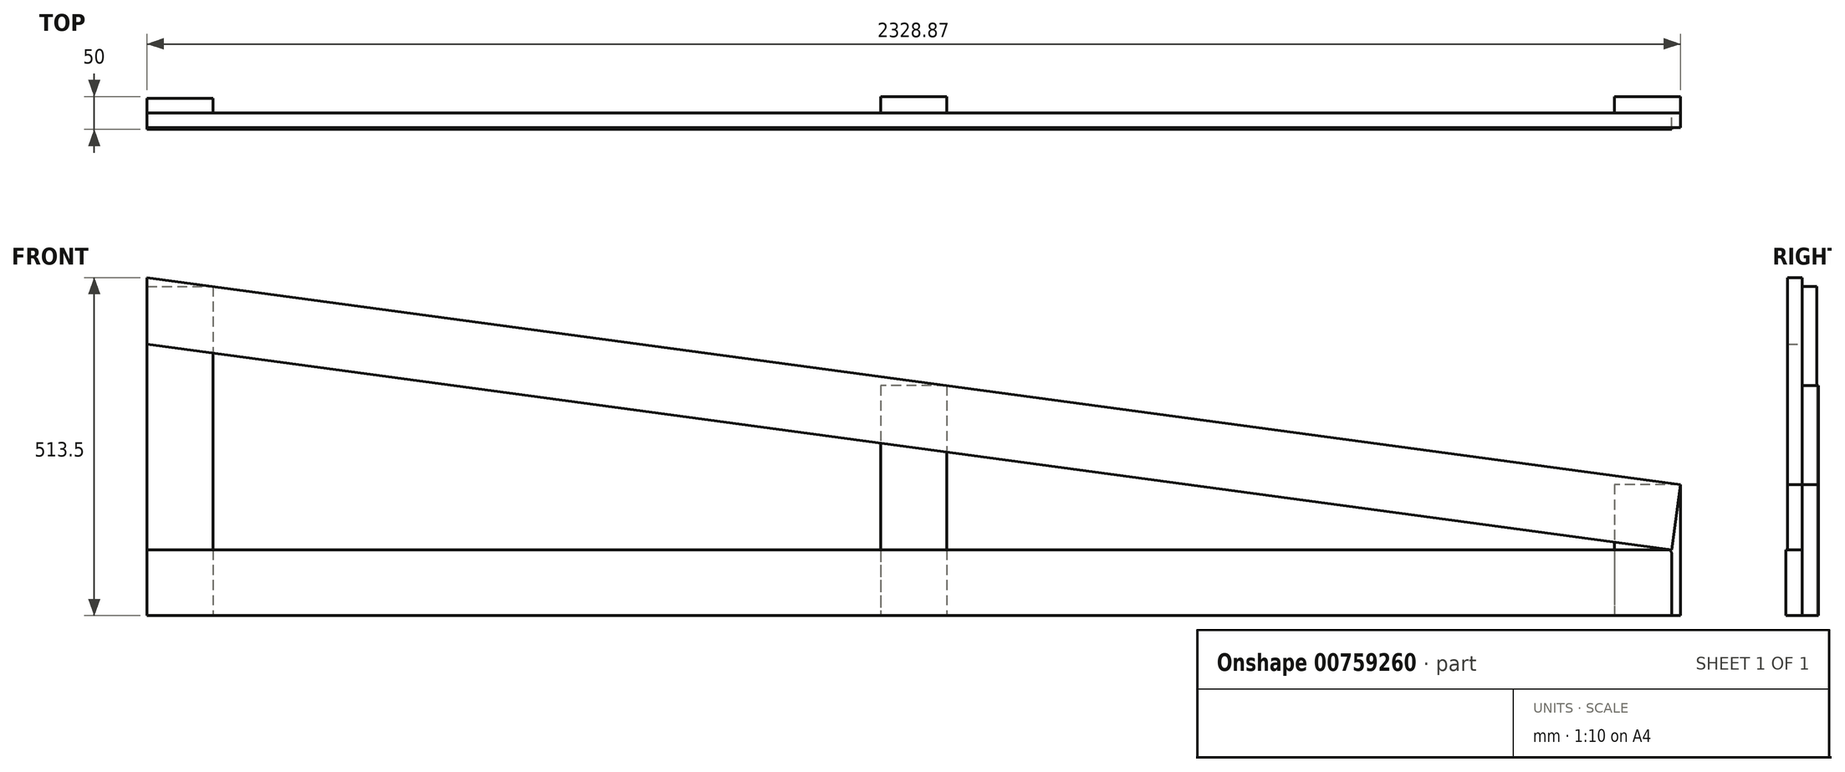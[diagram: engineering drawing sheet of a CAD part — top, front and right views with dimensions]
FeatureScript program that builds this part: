
annotation { "Feature Type Name" : "Feature", "Feature Type Description" : "" }
export const myFeature = defineFeature(function(context is Context, id is Id, definition is map)
    precondition{}
    {
        {
            var Q0;
            Q0=qCreatedBy(makeId("Front.planeOp"),FACE);
            var sketch = newSketch(context, id + "F0", { "sketchPlane" : qUnion([Q0])});
            skLineSegment(sketch, "E0.bottom", {"start": v(0, 500) * mm, "end": v(100, 500) * mm});
            skLineSegment(sketch, "E0.top", {"start": v(0, 0) * mm, "end": v(100, 0) * mm});
            skLineSegment(sketch, "E0.left", {"start": v(0, 500) * mm, "end": v(0, 0) * mm});
            skLineSegment(sketch, "E0.right", {"start": v(100, 500) * mm, "end": v(100, 0) * mm});
            skSolve(sketch);
        }
        {
            var Q0;
            Q0 = qSketchRegion(id + "F0", true);
            extrude(context, id + "F1", {"entities" : qUnion([Q0]), "depth" : 22 * mm, "offsetDistance" : 25 * mm});
        }
        {
            var Q0;
            Q0=makeQuery(id+"F1.opExtrude","CAP_FACE",FACE,{"disambiguationData":[OSD([sQuery(id+"F0.wireOp",EDGE,"E0.bottom"),sQuery(id+"F0.wireOp",EDGE,"E0.top"),sQuery(id+"F0.wireOp",EDGE,"E0.left"),sQuery(id+"F0.wireOp",EDGE,"E0.right")])],"isStart":false});
            var sketch = newSketch(context, id + "F2", { "sketchPlane" : qUnion([Q0])});
            skLineSegment(sketch, "E1", {"start": v(0, 412.6) * mm, "end": v(2315.5, 100) * mm});
            skLineSegment(sketch, "E2", {"start": v(2315.5, 100) * mm, "end": v(2328.87, 199.1) * mm});
            skLineSegment(sketch, "E3", {"start": v(2328.87, 199.1) * mm, "end": v(0, 513.5) * mm});
            skLineSegment(sketch, "E4", {"start": v(0, 513.5) * mm, "end": v(0, 412.6) * mm});
            skLineSegment(sketch, "E5", {"start": v(0, 0) * mm, "end": v(2315.5, 0) * mm});
            skPoint(sketch, "E5.endSnap0", {"position": v(50, 0) * mm});
            skLineSegment(sketch, "E6", {"start": v(2315.5, 0) * mm, "end": v(2315.5, 95) * mm});
            skLineSegment(sketch, "E7", {"start": v(2310.5, 100) * mm, "end": v(0, 100) * mm});
            skLineSegment(sketch, "E8", {"start": v(0, 100) * mm, "end": v(0, 0) * mm});
            skPoint(sketch, "E9.visualSharp", {"position": v(2315.5, 100) * mm});
            skArc(sketch, "E9.filletArc", {"start": v(2315.5, 95) * mm, "mid": v(2314.03, 98.54) * mm, "end": v(2310.5, 100) * mm});
            skSolve(sketch);
        }
        {
            var Q0;
            {var subQ0=sQuery(id+"F2.wireOp",EDGE,"E2");Q0=makeQuery(id+"F2.imprint","IMPRINT",FACE,{"disambiguationData":[TD([[makeQuery(id+"F2.imprint","IMPRINT",EDGE,{"derivedFrom":subQ0}),1.0]])]});}
            var Q1;
            {var subQ5=makeQuery(id+"F1.opExtrude","CAP_EDGE",EDGE,{"disambiguationData":[OSD([sQuery(id+"F0.wireOp",EDGE,"E0.bottom")])],"isStart":false});Q1=makeQuery(id+"F2.imprint","IMPRINT",FACE,{"disambiguationData":[TD([[makeQuery(id+"F2.imprint","IMPRINT",EDGE,{"derivedFrom":subQ5}),-1.0]])]});}
            var Q2;
            {var subQ1=makeQuery(id+"F1.opExtrude","CAP_EDGE",EDGE,{"disambiguationData":[OSD([sQuery(id+"F0.wireOp",EDGE,"E0.bottom")])],"isStart":false});Q2=makeQuery(id+"F2.imprint","IMPRINT",FACE,{"disambiguationData":[TD([[makeQuery(id+"F2.imprint","IMPRINT",EDGE,{"derivedFrom":subQ1}),1.0]])]});}
            extrude(context, id + "F3", {"entities" : qUnion([Q0, Q1, Q2]), "operationType" : NewBodyOperationType.ADD, "depth" : 22 * mm, "offsetDistance" : 25 * mm});
        }
        {
            var Q0;
            {var subQ0=sQuery(id+"F2.wireOp",EDGE,"E1");var subQ3=sQuery(id+"F2.wireOp",EDGE,"E3");var subQ4=sQuery(id+"F2.wireOp",EDGE,"E2");var subQ5=makeQuery(id+"F3.opExtrude","CAP_FACE",FACE,{"disambiguationData":[OSD([subQ0,subQ4,subQ3,sQuery(id+"F2.wireOp",EDGE,"E4")])],"isStart":true});Q0=makeQuery(id+"F3.boolean.opBoolean","SPLIT",FACE,{"disambiguationData":[TD([makeQuery(id+"F3.opExtrude","SWEPT_FACE",FACE,{"disambiguationData":[OSD([subQ0])]})])],"derivedFrom":subQ5});}
            var sketch = newSketch(context, id + "F4", { "sketchPlane" : qUnion([Q0])});
            skLineSegment(sketch, "E10.bottom", {"start": v(-1214.44, 349.55) * mm, "end": v(-1114.44, 349.55) * mm});
            skLineSegment(sketch, "E10.top", {"start": v(-1214.44, 0) * mm, "end": v(-1114.44, 0) * mm});
            skLineSegment(sketch, "E10.left", {"start": v(-1214.44, 349.55) * mm, "end": v(-1214.44, 0) * mm});
            skLineSegment(sketch, "E10.right", {"start": v(-1114.44, 349.55) * mm, "end": v(-1114.44, 0) * mm});
            skLineSegment(sketch, "E11.bottom", {"start": v(-2328.87, 199.1) * mm, "end": v(-2228.87, 199.1) * mm});
            skLineSegment(sketch, "E11.top", {"start": v(-2328.87, 0) * mm, "end": v(-2228.87, 0) * mm});
            skLineSegment(sketch, "E11.left", {"start": v(-2328.87, 199.1) * mm, "end": v(-2328.87, 0) * mm});
            skLineSegment(sketch, "E11.right", {"start": v(-2228.87, 199.1) * mm, "end": v(-2228.87, 0) * mm});
            skSolve(sketch);
        }
        {
            var Q0;
            Q0 = qSketchRegion(id + "F4", true);
            extrude(context, id + "F5", {"entities" : qUnion([Q0]), "operationType" : NewBodyOperationType.ADD, "depth" : 25 * mm, "offsetDistance" : 25 * mm});
        }
        {
            var Q0;
            {var subQ3=sQuery(id+"F2.wireOp",EDGE,"E6");Q0=makeQuery(id+"F2.imprint","IMPRINT",FACE,{"disambiguationData":[TD([[makeQuery(id+"F2.imprint","IMPRINT",EDGE,{"derivedFrom":subQ3}),1.0]])]});}
            var Q1;
            {var subQ0=sQuery(id+"F2.wireOp",EDGE,"E8");Q1=makeQuery(id+"F2.imprint","IMPRINT",FACE,{"disambiguationData":[TD([[makeQuery(id+"F2.imprint","IMPRINT",EDGE,{"derivedFrom":subQ0}),1.0]])]});}
            extrude(context, id + "F6", {"entities" : qUnion([Q0, Q1]), "operationType" : NewBodyOperationType.ADD, "depth" : 25 * mm, "offsetDistance" : 25 * mm});
        }
    });
